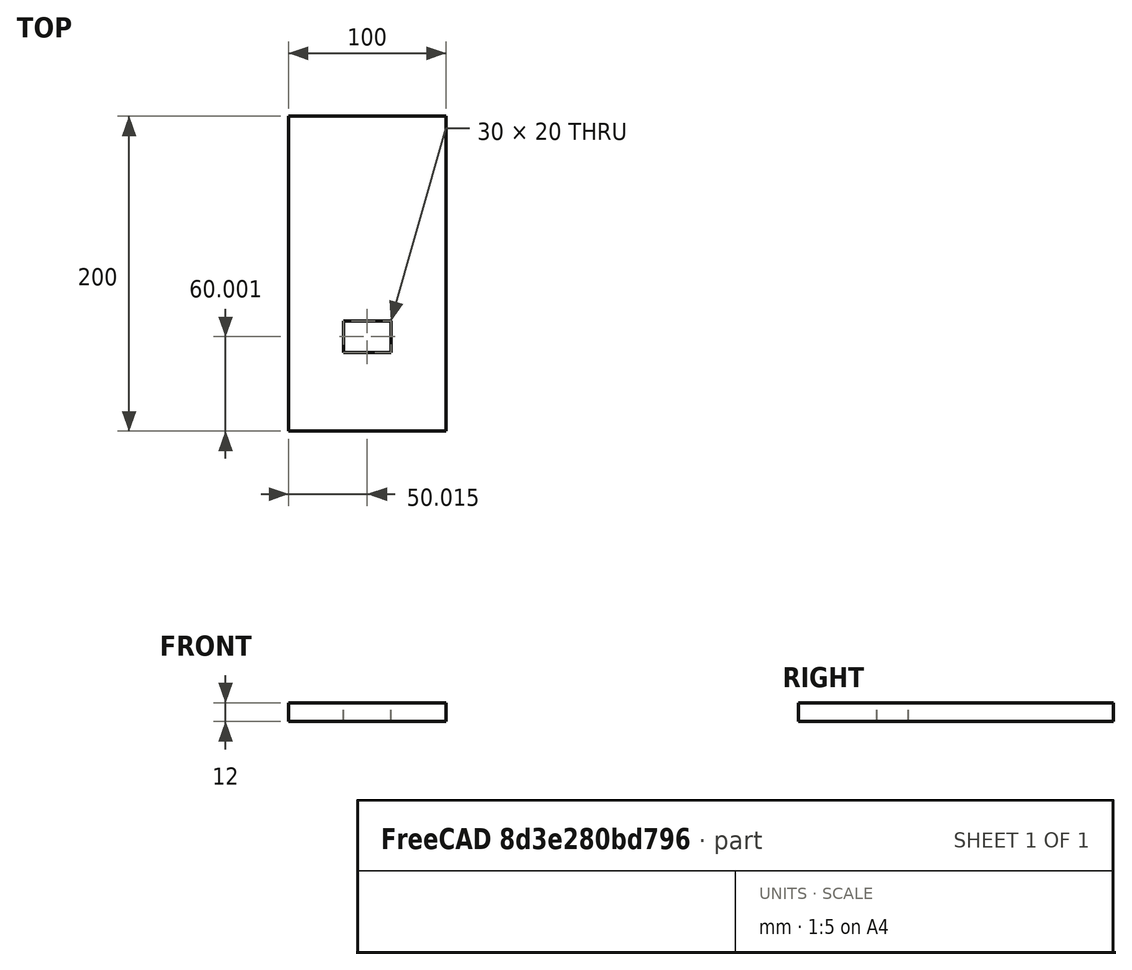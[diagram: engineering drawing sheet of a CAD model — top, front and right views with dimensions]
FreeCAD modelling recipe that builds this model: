
FCSTD DOCUMENT  (FreeCAD 0.16R6703 (Git))
Label: box2_back
License: All rights reserved
LicenseURL: http://en.wikipedia.org/wiki/All_rights_reserved
objects: Drawing::FeatureViewPython×7, Drawing::FeatureViewPart×2, PartDesign::Pad×1, Drawing::FeaturePage×1
note: 2 computed .brp shape members not serialized (recipe doc carries the construction recipe); baked Part::Feature solids carry a one-line shape summary decoded from their .brp

FEATURE [PartDesign::Pad] Pad
  Length = 12
  Length2 = 100
  Type = 0
FEATURE [Drawing::FeatureViewPart] Ortho  label="Ortho_0_0"
  Direction = (1,0,0)
  HiddenWidth = 0.15
  LineWidth = 0.35
  Rotation = -90
  Scale = 1.5
  ShowHiddenLines = false
  ShowSmoothLines = false
  Source = -> Pad
  Tolerance = 0.05
  ViewResult = <g id="Ortho_0_0"\n   transform="rotate(-90,129.104,44.3333) translate(129.104,44.3333) scale(1.5,1.5)"\n  >\n<g   stroke="rgb(0, 0, 0)"\n   stroke-width="0.233333"\n   stroke-linecap="butt"\n   stroke-linejoin="miter"\n   fill="none"\n   transform="scale(1,-1)"\n  >\n<path id= "1" d=" M 0 46.0692 L 12 46.0692 " />\n<path id= "2" d=" M 0 -153.931 L 12 -153.931 " />\n<path id= "3" d=" M 0 46.0692 L 0 -153.931 " />\n<path id= "4" d=" M 12 46.0692 L 12 -153.931 " />\n</g>\n</g>
  Visible = true
  X = 129.104
  Y = 44.3333
FEATURE [Drawing::FeatureViewPart] Ortho001  label="Ortho_0_-1"
  Direction = (0,0,-1)
  HiddenWidth = 0.15
  LineWidth = 0.35
  Rotation = 90
  Scale = 1.5
  ShowHiddenLines = false
  ShowSmoothLines = false
  Source = -> Pad
  Tolerance = 0.05
  ViewResult = <g id="Ortho_0_-1"\n   transform="rotate(90,129.104,171.374) translate(129.104,171.374) scale(1.5,1.5)"\n  >\n<g   stroke="rgb(0, 0, 0)"\n   stroke-width="0.233333"\n   stroke-linecap="butt"\n   stroke-linejoin="miter"\n   fill="none"\n   transform="scale(1,-1)"\n  >\n<path id= "1" d=" M 26.1948 -46.0692 L -73.8052 -46.0692 " />\n<path id= "2" d=" M -73.8052 -46.0692 L -73.8052 153.931 " />\n<path id= "3" d=" M -73.8052 153.931 L 26.1948 153.931 " />\n<path id= "4" d=" M 26.1948 153.931 L 26.1948 -46.0692 " />\n<path id= "5" d=" M -38.8248 3.93083 L -8.82479 3.93083 " />\n<path id= "6" d=" M -8.82479 3.93083 L -8.82479 23.9308 " />\n<path id= "7" d=" M -8.82479 23.9308 L -38.8248 23.9308 " />\n<path id= "8" d=" M -38.8248 23.9308 L -38.8248 3.93083 " />\n</g>\n</g>
  Visible = true
  X = 129.104
  Y = 171.374
FEATURE [Drawing::FeatureViewPython] dim001  # drawing view (typed FeaturePython)
  Rotation = 0
  ViewResult = <g> \n  <line x1="360.000500" y1="212.666200" x2="360.000500" y2="221.779221" style="stroke:rgb(0,0,255);stroke-width:0.50" />\n<line x1="60.000200" y1="212.666200" x2="60.000200" y2="221.779221" style="stroke:rgb(0,0,255);stroke-width:0.50" />\n<line x1="360.000500" y1="220.779221" x2="60.000200" y2="220.779221" style="stroke:rgb(0,0,255);stroke-width:0.50" /> \n  <polygon points="60.000200,220.779221 63.000200,221.779221 64.000200,220.779221 63.000200,219.779221" style="fill:rgb(0,0,255);stroke:rgb(0,0,255);stroke-width:0" /><polygon points="360.000500,220.779221 357.000500,219.779221 356.000500,220.779221 357.000500,221.779221" style="fill:rgb(0,0,255);stroke:rgb(0,0,255);stroke-width:0" /> \n  <text x="210.000350" y="218.779221" font-family="inherit" font-size="7" fill="rgb(0,0,255)" text-anchor="middle" transform="rotate(0.000000 210.000350,218.779221)" >200</text> </g>
  Visible = true
  X = 0
  Y = 0
  arrowL1 = 3
  arrowL2 = 1
  arrowW = 2
  arrow_scheme = 0
  autoPlaceOffset = 2
  autoPlaceText = true
  click1_x = 97.4131
  click1_y = 220.779
  click2_x = 97.4131
  click2_y = 220.779
  comma_decimal_place = false
  dimension_line_overshoot = 1
  gap_datum_points = 2
  halfDimension_linear = false
  lineColor = rgb(0,0,255)
  strokeWidth = 0.5
  textFormat_linear = %(value)3.3f
  textRenderer_color = rgb(0,0,255)
  textRenderer_family = inherit
  textRenderer_size = 7
  unit_custom_scale = 1
  unit_scheme = 0
FEATURE [Drawing::FeatureViewPython] dim002  # drawing view (typed FeaturePython)
  Rotation = 0
  ViewResult = <g> \n  <line x1="58.000200" y1="210.666200" x2="48.417571" y2="210.666200" style="stroke:rgb(0,0,255);stroke-width:0.50" />\n<line x1="58.000200" y1="60.666200" x2="48.417571" y2="60.666200" style="stroke:rgb(0,0,255);stroke-width:0.50" />\n<line x1="49.417571" y1="210.666200" x2="49.417571" y2="60.666200" style="stroke:rgb(0,0,255);stroke-width:0.50" /> \n  <polygon points="49.417571,60.666200 48.417571,63.666200 49.417571,64.666200 50.417571,63.666200" style="fill:rgb(0,0,255);stroke:rgb(0,0,255);stroke-width:0" /><polygon points="49.417571,210.666200 50.417571,207.666200 49.417571,206.666200 48.417571,207.666200" style="fill:rgb(0,0,255);stroke:rgb(0,0,255);stroke-width:0" /> \n  <text x="47.417571" y="135.666200" font-family="inherit" font-size="7" fill="rgb(0,0,255)" text-anchor="middle" transform="rotate(-90.000000 47.417571,135.666200)" >100</text> </g>
  Visible = true
  X = 0
  Y = 0
  arrowL1 = 3
  arrowL2 = 1
  arrowW = 2
  arrow_scheme = 0
  autoPlaceOffset = 2
  autoPlaceText = true
  click1_x = 49.4176
  click1_y = 147.542
  click2_x = 49.4176
  click2_y = 147.542
  comma_decimal_place = false
  dimension_line_overshoot = 1
  gap_datum_points = 2
  halfDimension_linear = false
  lineColor = rgb(0,0,255)
  strokeWidth = 0.5
  textFormat_linear = %(value)3.3f
  textRenderer_color = rgb(0,0,255)
  textRenderer_family = inherit
  textRenderer_size = 7
  unit_custom_scale = 1
  unit_scheme = 0
FEATURE [Drawing::FeatureViewPython] dim003  # drawing view (typed FeaturePython)
  Rotation = 0
  ViewResult = <g> \n  <line x1="58.000200" y1="44.333300" x2="47.706527" y2="44.333300" style="stroke:rgb(0,0,255);stroke-width:0.50" />\n<line x1="58.000200" y1="26.333300" x2="47.706527" y2="26.333300" style="stroke:rgb(0,0,255);stroke-width:0.50" />\n<line x1="48.706527" y1="44.333300" x2="48.706527" y2="26.333300" style="stroke:rgb(0,0,255);stroke-width:0.50" /> \n  <polygon points="48.706527,26.333300 47.706527,29.333300 48.706527,30.333300 49.706527,29.333300" style="fill:rgb(0,0,255);stroke:rgb(0,0,255);stroke-width:0" /><polygon points="48.706527,44.333300 49.706527,41.333300 48.706527,40.333300 47.706527,41.333300" style="fill:rgb(0,0,255);stroke:rgb(0,0,255);stroke-width:0" /> \n  <text x="46.706527" y="35.333300" font-family="inherit" font-size="7" fill="rgb(0,0,255)" text-anchor="middle" transform="rotate(-90.000000 46.706527,35.333300)" >12</text> </g>
  Visible = true
  X = 0
  Y = 0
  arrowL1 = 3
  arrowL2 = 1
  arrowW = 2
  arrow_scheme = 0
  autoPlaceOffset = 2
  autoPlaceText = true
  click1_x = 48.7065
  click1_y = 38.0409
  click2_x = 48.7065
  click2_y = 38.0409
  comma_decimal_place = false
  dimension_line_overshoot = 1
  gap_datum_points = 2
  halfDimension_linear = false
  lineColor = rgb(0,0,255)
  strokeWidth = 0.5
  textFormat_linear = %(value)3.3f
  textRenderer_color = rgb(0,0,255)
  textRenderer_family = inherit
  textRenderer_size = 7
  unit_custom_scale = 1
  unit_scheme = 0
FEATURE [Drawing::FeatureViewPython] dim006  # drawing view (typed FeaturePython)
  Rotation = 0
  ViewResult = <g> \n  <line x1="135.000245" y1="160.136815" x2="135.000245" y2="160.273898" style="stroke:rgb(0,0,255);stroke-width:0.50" />\n<line x1="60.000200" y1="208.666200" x2="60.000200" y2="158.273898" style="stroke:rgb(0,0,255);stroke-width:0.50" />\n<line x1="135.000245" y1="159.273898" x2="60.000200" y2="159.273898" style="stroke:rgb(0,0,255);stroke-width:0.50" /> \n  <polygon points="60.000200,159.273898 63.000200,160.273898 64.000200,159.273898 63.000200,158.273898" style="fill:rgb(0,0,255);stroke:rgb(0,0,255);stroke-width:0" /><polygon points="135.000245,159.273898 132.000245,158.273898 131.000245,159.273898 132.000245,160.273898" style="fill:rgb(0,0,255);stroke:rgb(0,0,255);stroke-width:0" /> \n  <text x="97.500223" y="157.273898" font-family="inherit" font-size="7" fill="rgb(0,0,255)" text-anchor="middle" transform="rotate(0.000000 97.500223,157.273898)" >50</text> </g>
  Visible = true
  X = 0
  Y = 0
  arrowL1 = 3
  arrowL2 = 1
  arrowW = 2
  arrow_scheme = 0
  autoPlaceOffset = 2
  autoPlaceText = true
  click1_x = 86.7474
  click1_y = 159.274
  click2_x = 86.7474
  click2_y = 159.274
  comma_decimal_place = false
  dimension_line_overshoot = 1
  gap_datum_points = 2
  halfDimension_linear = false
  lineColor = rgb(0,0,255)
  strokeWidth = 0.5
  textFormat_linear = %(value)3.3f
  textRenderer_color = rgb(0,0,255)
  textRenderer_family = inherit
  textRenderer_size = 7
  unit_custom_scale = 1
  unit_scheme = 0
FEATURE [Drawing::FeatureViewPython] dim007  # drawing view (typed FeaturePython)
  Rotation = 0
  ViewResult = <g> \n  <line x1="137.000245" y1="158.136815" x2="137.164962" y2="158.136815" style="stroke:rgb(0,0,255);stroke-width:0.50" />\n<line x1="62.000200" y1="210.666200" x2="137.164962" y2="210.666200" style="stroke:rgb(0,0,255);stroke-width:0.50" />\n<line x1="136.164962" y1="158.136815" x2="136.164962" y2="210.666200" style="stroke:rgb(0,0,255);stroke-width:0.50" /> \n  <polygon points="136.164962,210.666200 137.164962,207.666200 136.164962,206.666200 135.164962,207.666200" style="fill:rgb(0,0,255);stroke:rgb(0,0,255);stroke-width:0" /><polygon points="136.164962,158.136815 135.164962,161.136815 136.164962,162.136815 137.164962,161.136815" style="fill:rgb(0,0,255);stroke:rgb(0,0,255);stroke-width:0" /> \n  <text x="134.164962" y="184.401508" font-family="inherit" font-size="7" fill="rgb(0,0,255)" text-anchor="middle" transform="rotate(-90.000000 134.164962,184.401508)" >35.02</text> </g>
  Visible = true
  X = 0
  Y = 0
  arrowL1 = 3
  arrowL2 = 1
  arrowW = 2
  arrow_scheme = 0
  autoPlaceOffset = 2
  autoPlaceText = true
  click1_x = 136.165
  click1_y = 182.738
  click2_x = 136.165
  click2_y = 182.738
  comma_decimal_place = false
  dimension_line_overshoot = 1
  gap_datum_points = 2
  halfDimension_linear = false
  lineColor = rgb(0,0,255)
  strokeWidth = 0.5
  textFormat_linear = %(value)3.3f
  textRenderer_color = rgb(0,0,255)
  textRenderer_family = inherit
  textRenderer_size = 7
  unit_custom_scale = 1
  unit_scheme = 0
FEATURE [Drawing::FeatureViewPython] dim004  # drawing view (typed FeaturePython)
  Rotation = 0
  ViewResult = <g> \n  <line x1="167.000200" y1="158.136815" x2="181.605224" y2="158.136815" style="stroke:rgb(0,0,255);stroke-width:0.50" />\n<line x1="167.000200" y1="113.136800" x2="181.605224" y2="113.136800" style="stroke:rgb(0,0,255);stroke-width:0.50" />\n<line x1="180.605224" y1="158.136815" x2="180.605224" y2="113.136800" style="stroke:rgb(0,0,255);stroke-width:0.50" /> \n  <polygon points="180.605224,113.136800 179.605224,116.136800 180.605224,117.136800 181.605224,116.136800" style="fill:rgb(0,0,255);stroke:rgb(0,0,255);stroke-width:0" /><polygon points="180.605224,158.136815 181.605224,155.136815 180.605224,154.136815 179.605224,155.136815" style="fill:rgb(0,0,255);stroke:rgb(0,0,255);stroke-width:0" /> \n  <text x="178.605224" y="135.636807" font-family="inherit" font-size="7" fill="rgb(0,0,255)" text-anchor="middle" transform="rotate(-90.000000 178.605224,135.636807)" >30</text> </g>
  Visible = true
  X = 0
  Y = 0
  arrowL1 = 3
  arrowL2 = 1
  arrowW = 2
  arrow_scheme = 0
  autoPlaceOffset = 2
  autoPlaceText = true
  click1_x = 180.605
  click1_y = 132.254
  click2_x = 180.605
  click2_y = 132.254
  comma_decimal_place = false
  dimension_line_overshoot = 1
  gap_datum_points = 2
  halfDimension_linear = false
  lineColor = rgb(0,0,255)
  strokeWidth = 0.5
  textFormat_linear = %(value)3.3f
  textRenderer_color = rgb(0,0,255)
  textRenderer_family = inherit
  textRenderer_size = 7
  unit_custom_scale = 1
  unit_scheme = 0
FEATURE [Drawing::FeatureViewPython] dim005  # drawing view (typed FeaturePython)
  Rotation = 0
  ViewResult = <g> \n  <line x1="165.000200" y1="111.136800" x2="165.000200" y2="98.901709" style="stroke:rgb(0,0,255);stroke-width:0.50" />\n<line x1="135.000245" y1="111.136800" x2="135.000245" y2="98.901709" style="stroke:rgb(0,0,255);stroke-width:0.50" />\n<line x1="165.000200" y1="99.901709" x2="135.000245" y2="99.901709" style="stroke:rgb(0,0,255);stroke-width:0.50" /> \n  <polygon points="135.000245,99.901709 138.000245,100.901709 139.000245,99.901709 138.000245,98.901709" style="fill:rgb(0,0,255);stroke:rgb(0,0,255);stroke-width:0" /><polygon points="165.000200,99.901709 162.000200,98.901709 161.000200,99.901709 162.000200,100.901709" style="fill:rgb(0,0,255);stroke:rgb(0,0,255);stroke-width:0" /> \n  <text x="150.000223" y="97.901709" font-family="inherit" font-size="7" fill="rgb(0,0,255)" text-anchor="middle" transform="rotate(0.000000 150.000223,97.901709)" >20</text> </g>
  Visible = true
  X = 0
  Y = 0
  arrowL1 = 3
  arrowL2 = 1
  arrowW = 2
  arrow_scheme = 0
  autoPlaceOffset = 2
  autoPlaceText = true
  click1_x = 143.986
  click1_y = 99.9017
  click2_x = 143.986
  click2_y = 99.9017
  comma_decimal_place = false
  dimension_line_overshoot = 1
  gap_datum_points = 2
  halfDimension_linear = false
  lineColor = rgb(0,0,255)
  strokeWidth = 0.5
  textFormat_linear = %(value)3.3f
  textRenderer_color = rgb(0,0,255)
  textRenderer_family = inherit
  textRenderer_size = 7
  unit_custom_scale = 1
  unit_scheme = 0
FEATURE [Drawing::FeaturePage] Page
  EditableTexts = AUTHOR NAME | CREATION DATE | SUPERVISOR NAME | CHECK DATE | SCALE | WEIGHT | NUMBER | SHEET | Box 2 Back | SUBTITLE
  Group = -> [Ortho,Ortho001,dim001,dim002,dim003,dim006,dim007,dim004,dim005]
